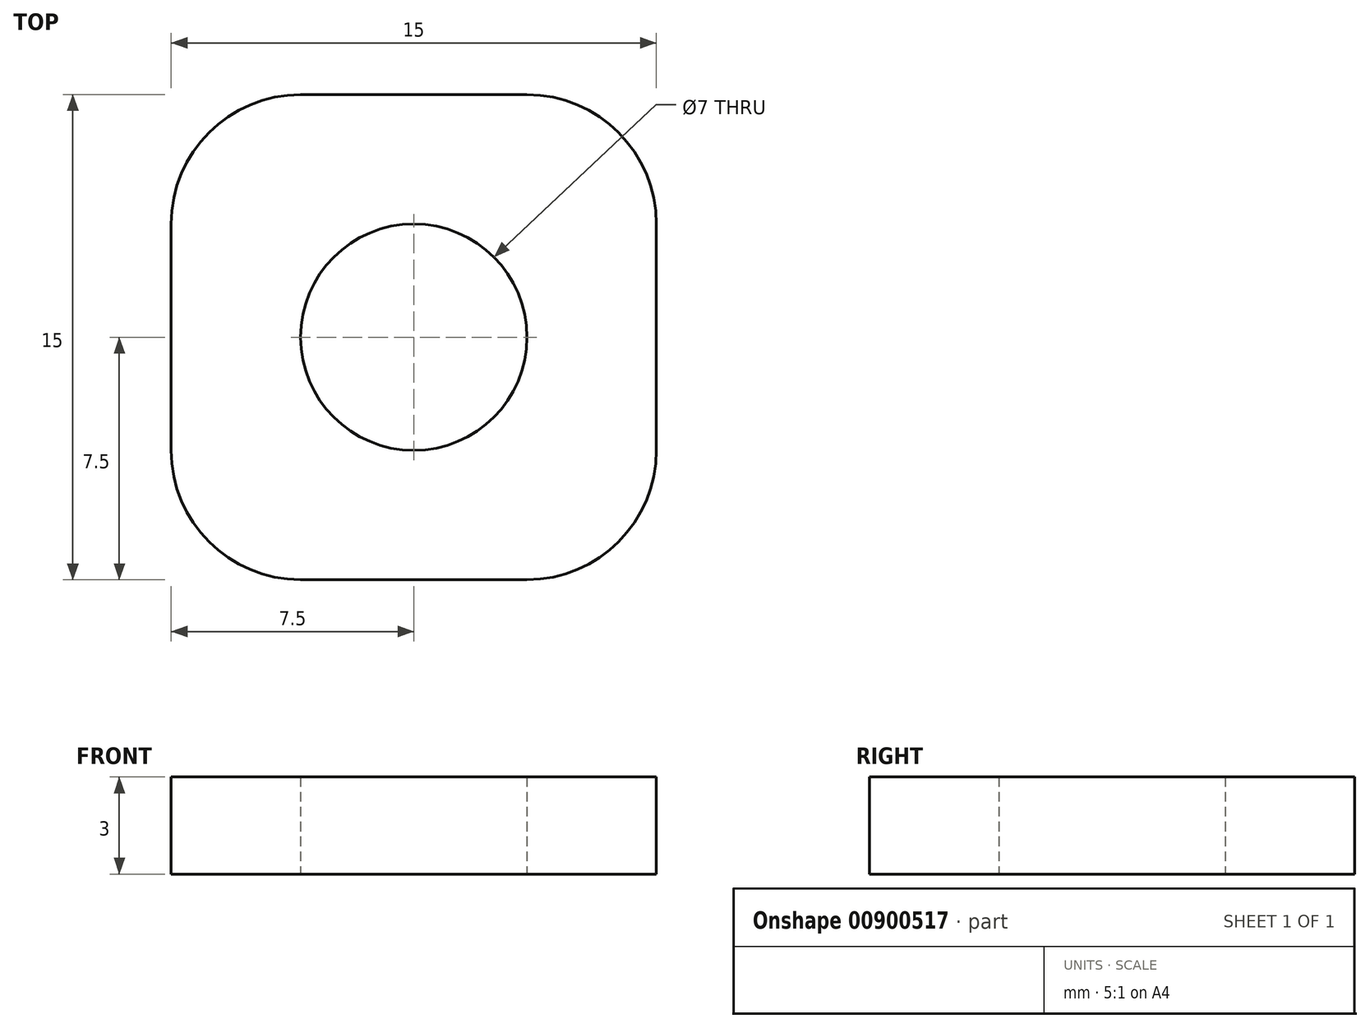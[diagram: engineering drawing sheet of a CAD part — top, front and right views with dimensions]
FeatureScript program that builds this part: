
annotation { "Feature Type Name" : "Feature", "Feature Type Description" : "" }
export const myFeature = defineFeature(function(context is Context, id is Id, definition is map)
    precondition{}
    {
        {
            var Q0;
            Q0=qCreatedBy(makeId("Top.planeOp"),FACE);
            var sketch = newSketch(context, id + "F0", { "sketchPlane" : qUnion([Q0])});
            skLineSegment(sketch, "E0.bottom", {"start": v(7.5, 7.5) * mm, "end": v(-7.5, 7.5) * mm});
            skLineSegment(sketch, "E0.top", {"start": v(7.5, -7.5) * mm, "end": v(-7.5, -7.5) * mm});
            skLineSegment(sketch, "E0.left", {"start": v(7.5, 7.5) * mm, "end": v(7.5, -7.5) * mm});
            skLineSegment(sketch, "E0.right", {"start": v(-7.5, 7.5) * mm, "end": v(-7.5, -7.5) * mm});
            skPoint(sketch, "E0.middle", {"position": v(0, 0) * mm});
            skCircle(sketch, "E1", {"center": v(0, 0) * mm, "radius": 3.5 * mm});
            skSolve(sketch);
        }
        {
            var Q0;
            Q0=makeQuery(id+"F0.imprint","IMPRINT",FACE,{"disambiguationData":[TD([[makeQuery(id+"F0.imprint","IMPRINT",EDGE,{"derivedFrom":sQuery(id+"F0.wireOp",EDGE,"E0.bottom")}),1.0]])]});
            extrude(context, id + "F1", {"entities" : qUnion([Q0]), "depth" : 3 * mm, "offsetDistance" : 25 * mm});
        }
        {
            var Q0;
            Q0=makeQuery(id+"F1.opExtrude","SWEPT_EDGE",EDGE,{"disambiguationData":[OSD([sQuery(id+"F0.wireOp",EDGE,"E0.bottom"),sQuery(id+"F0.wireOp",EDGE,"E0.right")])]});
            var Q1;
            Q1=makeQuery(id+"F1.opExtrude","SWEPT_EDGE",EDGE,{"disambiguationData":[OSD([sQuery(id+"F0.wireOp",EDGE,"E0.top"),sQuery(id+"F0.wireOp",EDGE,"E0.right")])]});
            var Q2;
            Q2=makeQuery(id+"F1.opExtrude","SWEPT_EDGE",EDGE,{"disambiguationData":[OSD([sQuery(id+"F0.wireOp",EDGE,"E0.top"),sQuery(id+"F0.wireOp",EDGE,"E0.left")])]});
            var Q3;
            Q3=makeQuery(id+"F1.opExtrude","SWEPT_EDGE",EDGE,{"disambiguationData":[OSD([sQuery(id+"F0.wireOp",EDGE,"E0.bottom"),sQuery(id+"F0.wireOp",EDGE,"E0.left")])]});
            fillet(context, id + "F2", {"entities" : qUnion([Q0, Q1, Q2, Q3]), "radius" : 4 * mm, "tangentPropagation" : true, "allowEdgeOverflow" : false});
        }
    });
